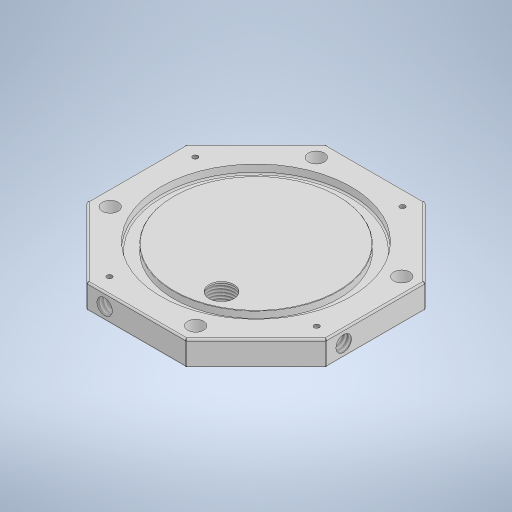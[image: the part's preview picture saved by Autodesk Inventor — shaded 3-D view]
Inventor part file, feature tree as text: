
AUTODESK INVENTOR PART (.ipt)
format: ipt  version: 2024.3 (Build 283343000, 343)  size: 395,264 bytes
history: native  units: in
note: dims shown in document units (in); Inventor stores cm internally (conversion verified against a paired STEP export)
features: sketch x6, hole x5, extrude x3, pattern_circular x3, fillet x3, other x1
ambient origin geometry x8: Origin, YZ Plane, XZ Plane, XY Plane, X Axis, Y Axis, Z Axis, Center Point
bodies: Solid1 (feature_tree)
feature tree (21):
  other  "Clippard 8-MC heart v2A.ipt"
  extrude  "Ex1: base"  TaperAngle=0.0deg  [1 undecoded]
  hole  "Hole: Flange screws"  [1 undecoded]
  pattern_circular  "Circular Pattern: Flange screws"  [2 undecoded]
  sketch  "Sketch: O-ring (#227)"  dims[d6=0.094in d7=0.385in d8=0.25in d9=0.6871in d10=0.15in d11=0.0in]
  extrude  "Ex: O-ring groove (for #227 o-ring)"  Depth=0.0625in
  extrude  "Ex: Air cutout"  Depth=0.0625in
  fillet  "Fillet1: O-ring groove"  Radius=0.75in
  fillet  "Fillet2: O-ring groove"  Radius=0.8108in
  fillet  "Fillet3: outside edges"  Radius=0.0625in
  hole  "Hole: Air input"  [1 undecoded]
  hole  "Hole: PCB screws"  [1 undecoded]
  hole  "Hole: Mounting hole (top)"  [1 undecoded]
  hole  "Hole: Mounting holes (side)"  [1 undecoded]
  pattern_circular  "Circular Pattern: PCB screws"  [2 undecoded]
  pattern_circular  "Circular Pattern: Mounting holes (side)"  [2 undecoded]
  sketch  "Sketch2: top flange"  dims[d24=0.313in d25=0.273in d26=0.0246in d27=0.3269in d28=0.375in d29=0.25in d30=0.5635in d31=1.0in d32=0.0in]
  sketch  "Sketch: Flange screws"  dims[d33=0.196in d34=0.5in d35=0.375in d36=0.25in d37=0.5635in d39=0.0in]
  sketch  "Sketch3: Air input"  dims[d49=67.5deg d50=1.3in]
  sketch  "Sketch: PCB screws"  dims[d51=0.5385in]
  sketch  "Sketch: Mounting holes (side)"  dims[d52=0.2312in d53=0.2165in d54=0.4477in d55=0.0667in d56=0.172in d57=0.375in d58=0.25in d59=0.5635in d60=0.261in d61=0.0in d66=0.196in d67=0.5in d68=0.375in d69=0.25in d70=0.5635in d38=0.375in d40=0.75in d41=0.8108in d42=0.0625in d43=0.75in d44=0.375in]
note: 12 required parameter values undecoded (feature->parameter linkage not recoverable at this tier; creation-order binding heuristic only, values carry confidence <= 0.55)
